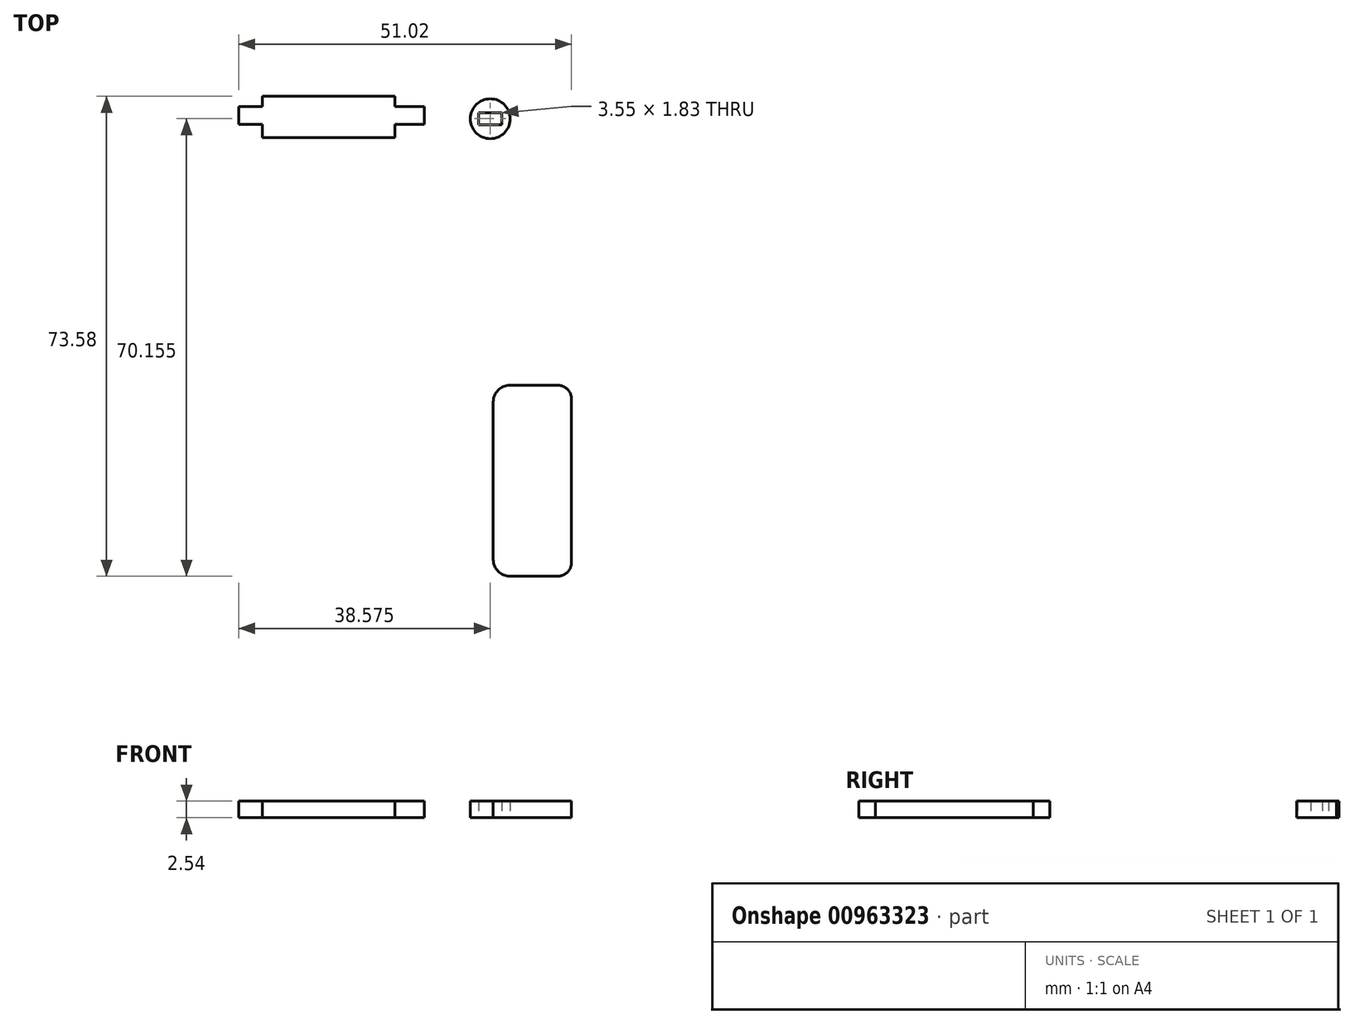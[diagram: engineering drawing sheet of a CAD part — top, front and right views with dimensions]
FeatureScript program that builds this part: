
annotation { "Feature Type Name" : "Feature", "Feature Type Description" : "" }
export const myFeature = defineFeature(function(context is Context, id is Id, definition is map)
    precondition{}
    {
        {
            var Q0;
            Q0=qCreatedBy(makeId("Top.planeOp"),FACE);
            var sketch = newSketch(context, id + "F0", { "sketchPlane" : qUnion([Q0])});
            skLineSegment(sketch, "E0.bottom", {"start": v(-2.08, 14.64) * mm, "end": v(-9.4, 14.64) * mm});
            skPoint(sketch, "E1.visualSharp", {"position": v(-11.95, 14.64) * mm});
            skArc(sketch, "E1.filletArc", {"start": v(-9.4, 14.64) * mm, "mid": v(-11.2, 13.9) * mm, "end": v(-11.95, 12.1) * mm});
            skArc(sketch, "E2.MirrorCS", {"start": v(-9.4, -14.64) * mm, "mid": v(-11.2, -13.9) * mm, "end": v(-11.95, -12.1) * mm});
            skLineSegment(sketch, "E3.MirrorCS", {"start": v(-2.08, -14.64) * mm, "end": v(-9.4, -14.64) * mm});
            skLineSegment(sketch, "E4", {"start": v(-11.95, 12.1) * mm, "end": v(-11.95, -12.1) * mm});
            skArc(sketch, "E5", {"start": v(0, 12.1) * mm, "mid": v(-0.44, 13.86) * mm, "end": v(-2.08, 14.64) * mm});
            skLineSegment(sketch, "E6", {"start": v(0, 12.1) * mm, "end": v(0, -12.1) * mm});
            skArc(sketch, "E7", {"start": v(-2.08, -14.64) * mm, "mid": v(-0.44, -13.86) * mm, "end": v(0, -12.1) * mm});
            skLineSegment(sketch, "E8", {"start": v(-47.33, 58.94) * mm, "end": v(-27, 58.94) * mm});
            skLineSegment(sketch, "E9", {"start": v(-27, 52.59) * mm, "end": v(-47.33, 52.59) * mm});
            skLineSegment(sketch, "E10", {"start": v(-47.33, 57.36) * mm, "end": v(-50.98, 57.36) * mm});
            skLineSegment(sketch, "E11", {"start": v(-50.98, 57.36) * mm, "end": v(-50.98, 54.66) * mm});
            skLineSegment(sketch, "E12", {"start": v(-50.98, 54.66) * mm, "end": v(-47.33, 54.66) * mm});
            skLineSegment(sketch, "E13", {"start": v(-22.49, 57.36) * mm, "end": v(-22.49, 54.66) * mm});
            skLineSegment(sketch, "E14", {"start": v(-27, 57.36) * mm, "end": v(-22.49, 57.36) * mm});
            skLineSegment(sketch, "E15", {"start": v(-22.49, 54.66) * mm, "end": v(-27, 54.66) * mm});
            skLineSegment(sketch, "E16", {"start": v(-47.33, 58.94) * mm, "end": v(-47.33, 57.36) * mm});
            skLineSegment(sketch, "E17", {"start": v(-47.33, 54.66) * mm, "end": v(-47.33, 52.59) * mm});
            skLineSegment(sketch, "E18", {"start": v(-27, 58.94) * mm, "end": v(-27, 57.36) * mm});
            skLineSegment(sketch, "E19", {"start": v(-27, 54.66) * mm, "end": v(-27, 52.59) * mm});
            skCircle(sketch, "E20", {"center": v(-12.4, 55.5) * mm, "radius": 3.06 * mm});
            skLineSegment(sketch, "E21.bottom", {"start": v(-14.18, 56.43) * mm, "end": v(-10.63, 56.43) * mm});
            skLineSegment(sketch, "E21.top", {"start": v(-14.18, 54.6) * mm, "end": v(-10.63, 54.6) * mm});
            skLineSegment(sketch, "E21.left", {"start": v(-14.18, 56.43) * mm, "end": v(-14.18, 54.6) * mm});
            skLineSegment(sketch, "E21.right", {"start": v(-10.63, 56.43) * mm, "end": v(-10.63, 54.6) * mm});
            skSolve(sketch);
        }
        {
            var Q0;
            Q0 = qSketchRegion(id + "F0", true);
            extrude(context, id + "F1", {"entities" : qUnion([Q0]), "depth" : 2.54 * mm, "offsetDistance" : 25.4 * mm});
        }
    });
